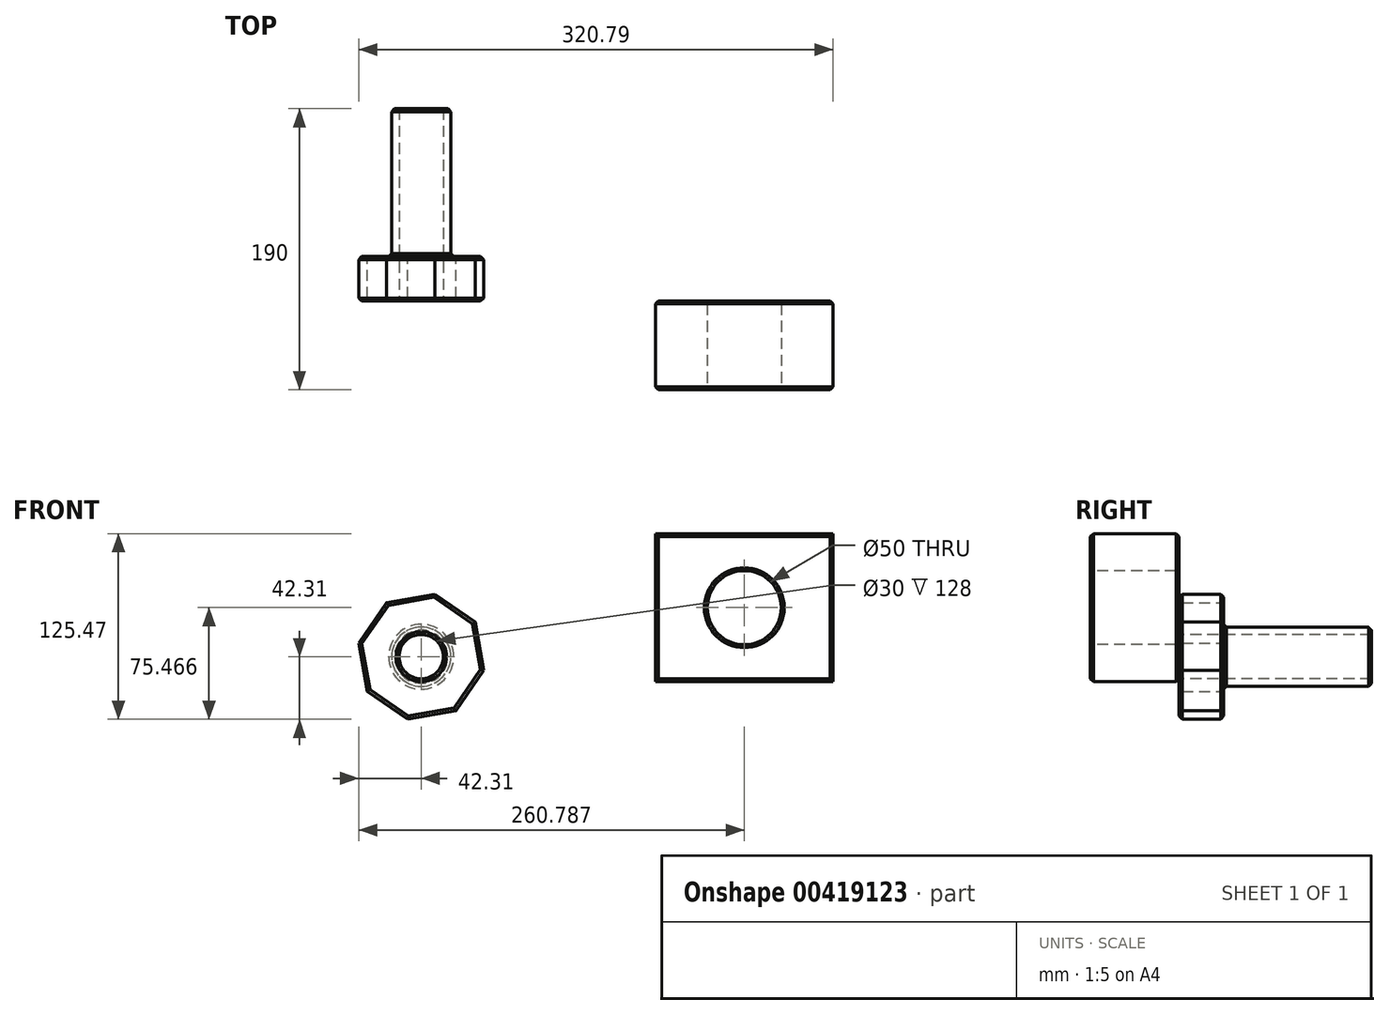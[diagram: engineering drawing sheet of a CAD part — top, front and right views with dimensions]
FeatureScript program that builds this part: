
annotation { "Feature Type Name" : "Feature", "Feature Type Description" : "" }
export const myFeature = defineFeature(function(context is Context, id is Id, definition is map)
    precondition{}
    {
        {
            var Q0;
            Q0=qCreatedBy(makeId("Front.planeOp"),FACE);
            var sketch = newSketch(context, id + "F0", { "sketchPlane" : qUnion([Q0])});
            skCircle(sketch, "E0.cCircle", {"center": v(0, 0) * mm, "radius": 40 * mm, "construction": true});
            skLineSegment(sketch, "E0.0", {"start": v(-42.31, 9.18) * mm, "end": v(-23.43, 36.4) * mm});
            skLineSegment(sketch, "E0.1", {"start": v(-23.43, 36.4) * mm, "end": v(9.18, 42.31) * mm});
            skLineSegment(sketch, "E0.2", {"start": v(9.18, 42.31) * mm, "end": v(36.4, 23.43) * mm});
            skLineSegment(sketch, "E0.3", {"start": v(36.4, 23.43) * mm, "end": v(42.31, -9.18) * mm});
            skLineSegment(sketch, "E0.4", {"start": v(42.31, -9.18) * mm, "end": v(23.43, -36.4) * mm});
            skLineSegment(sketch, "E0.5", {"start": v(23.43, -36.4) * mm, "end": v(-9.18, -42.31) * mm});
            skLineSegment(sketch, "E0.6", {"start": v(-9.18, -42.31) * mm, "end": v(-36.4, -23.43) * mm});
            skLineSegment(sketch, "E0.7", {"start": v(-36.4, -23.43) * mm, "end": v(-42.31, 9.18) * mm});
            skPoint(sketch, "E0.0.midPoint", {"position": v(-32.87, 22.8) * mm});
            skSolve(sketch);
        }
        {
            var Q0;
            Q0=makeQuery(id+"F0.imprint","IMPRINT",FACE,{"disambiguationData":[TD([[makeQuery(id+"F0.imprint","IMPRINT",EDGE,{"derivedFrom":sQuery(id+"F0.wireOp",EDGE,"E0.0")}),-1.0]])]});
            extrude(context, id + "F1", {"entities" : qUnion([Q0]), "depth" : 30 * mm});
        }
        {
            var Q0;
            Q0=makeQuery(id+"F1.opExtrude","CAP_FACE",FACE,{"disambiguationData":[OSD([sQuery(id+"F0.wireOp",EDGE,"E0.0"),sQuery(id+"F0.wireOp",EDGE,"E0.1"),sQuery(id+"F0.wireOp",EDGE,"E0.2"),sQuery(id+"F0.wireOp",EDGE,"E0.3"),sQuery(id+"F0.wireOp",EDGE,"E0.4"),sQuery(id+"F0.wireOp",EDGE,"E0.5"),sQuery(id+"F0.wireOp",EDGE,"E0.6"),sQuery(id+"F0.wireOp",EDGE,"E0.7")])],"isStart":true});
            var sketch = newSketch(context, id + "F2", { "sketchPlane" : qUnion([Q0])});
            skCircle(sketch, "E1", {"center": v(0, 0) * mm, "radius": 20 * mm});
            skSolve(sketch);
        }
        {
            var Q0;
            Q0=makeQuery(id+"F2.imprint","IMPRINT",FACE,{"disambiguationData":[TD([[makeQuery(id+"F2.imprint","IMPRINT",EDGE,{"derivedFrom":sQuery(id+"F2.wireOp",EDGE,"E1")}),1.0]])]});
            extrude(context, id + "F3", {"entities" : qUnion([Q0]), "operationType" : NewBodyOperationType.ADD, "depth" : 100 * mm});
        }
        {
            var Q0;
            Q0=makeQuery(id+"F1.opExtrude","CAP_FACE",FACE,{"disambiguationData":[OSD([sQuery(id+"F0.wireOp",EDGE,"E0.0"),sQuery(id+"F0.wireOp",EDGE,"E0.1"),sQuery(id+"F0.wireOp",EDGE,"E0.2"),sQuery(id+"F0.wireOp",EDGE,"E0.3"),sQuery(id+"F0.wireOp",EDGE,"E0.4"),sQuery(id+"F0.wireOp",EDGE,"E0.5"),sQuery(id+"F0.wireOp",EDGE,"E0.6"),sQuery(id+"F0.wireOp",EDGE,"E0.7")])],"isStart":false});
            var sketch = newSketch(context, id + "F4", { "sketchPlane" : qUnion([Q0])});
            skPoint(sketch, "E2", {"position": v(0, 0) * mm});
            skCircle(sketch, "E3", {"center": v(0, 0) * mm, "radius": 32.5 * mm});
            skSolve(sketch);
        }
        {
            var Q0;
            Q0=sQuery(id+"F4.wireOp",VERTEX,"E2");
            var Q1;
            Q1=makeQuery(id+"F1.opExtrude","SWEPT_BODY",BODY,{"disambiguationData":[OSD([sQuery(id+"F0.wireOp",EDGE,"E0.0"),sQuery(id+"F0.wireOp",EDGE,"E0.1"),sQuery(id+"F0.wireOp",EDGE,"E0.2"),sQuery(id+"F0.wireOp",EDGE,"E0.3"),sQuery(id+"F0.wireOp",EDGE,"E0.4"),sQuery(id+"F0.wireOp",EDGE,"E0.5"),sQuery(id+"F0.wireOp",EDGE,"E0.6"),sQuery(id+"F0.wireOp",EDGE,"E0.7")])]});
            hole(context, id + "F5", {"style" : HoleStyle.SIMPLE, "endStyle" : HoleEndStyle.THROUGH, "holeDiameter" : 30 * mm, "isTappedThrough" : true, "tappedDepth" : 12 * mm, "tapClearance" : 3, "locations" : qUnion([Q0]), "scope" : qUnion([Q1])});
        }
        {
            var Q0;
            Q0=makeQuery(id+"F5.hole-0.boolean.opBoolean","INTERSECT",EDGE,{"derivedFrom":[makeQuery(id+"F3.opExtrude","CAP_FACE",FACE,{"disambiguationData":[OSD([sQuery(id+"F2.wireOp",EDGE,"E1")])],"isStart":false}),makeQuery(id+"F5.hole-0.opRevolve","SWEPT_FACE",FACE,{"disambiguationData":[OSD([sQuery(id+"F5.hole-0.sketch.wireOp",EDGE,"core_line_2")])]})]});
            var Q1;
            Q1=makeQuery(id+"F3.opExtrude","CAP_EDGE",EDGE,{"disambiguationData":[OSD([sQuery(id+"F2.wireOp",EDGE,"E1")])],"isStart":false});
            chamfer(context, id + "F6", {"entities" : qUnion([Q0, Q1]), "width" : 2 * mm, "tangentPropagation" : true});
        }
        {
            var Q0;
            Q0=makeQuery(id+"F1.opExtrude","CAP_FACE",FACE,{"disambiguationData":[OSD([sQuery(id+"F0.wireOp",EDGE,"E0.0"),sQuery(id+"F0.wireOp",EDGE,"E0.1"),sQuery(id+"F0.wireOp",EDGE,"E0.2"),sQuery(id+"F0.wireOp",EDGE,"E0.3"),sQuery(id+"F0.wireOp",EDGE,"E0.4"),sQuery(id+"F0.wireOp",EDGE,"E0.5"),sQuery(id+"F0.wireOp",EDGE,"E0.6"),sQuery(id+"F0.wireOp",EDGE,"E0.7")])],"isStart":false});
            var sketch = newSketch(context, id + "F7", { "sketchPlane" : qUnion([Q0])});
            skLineSegment(sketch, "E4.bottom", {"start": v(158.48, 83.16) * mm, "end": v(278.48, 83.16) * mm});
            skLineSegment(sketch, "E4.top", {"start": v(158.48, -16.84) * mm, "end": v(278.48, -16.84) * mm});
            skLineSegment(sketch, "E4.left", {"start": v(158.48, 83.16) * mm, "end": v(158.48, -16.84) * mm});
            skLineSegment(sketch, "E4.right", {"start": v(278.48, 83.16) * mm, "end": v(278.48, -16.84) * mm});
            skSolve(sketch);
        }
        {
            var Q0;
            Q0=makeQuery(id+"F7.imprint","IMPRINT",FACE,{"disambiguationData":[TD([[makeQuery(id+"F7.imprint","IMPRINT",EDGE,{"derivedFrom":sQuery(id+"F7.wireOp",EDGE,"E4.bottom")}),-1.0]])]});
            extrude(context, id + "F8", {"entities" : qUnion([Q0]), "depth" : 60 * mm});
        }
        {
            var Q0;
            Q0=makeQuery(id+"F8.opExtrude","CAP_FACE",FACE,{"disambiguationData":[OSD([sQuery(id+"F7.wireOp",EDGE,"E4.bottom"),sQuery(id+"F7.wireOp",EDGE,"E4.top"),sQuery(id+"F7.wireOp",EDGE,"E4.left"),sQuery(id+"F7.wireOp",EDGE,"E4.right")])],"isStart":false});
            var sketch = newSketch(context, id + "F9", { "sketchPlane" : qUnion([Q0])});
            skPoint(sketch, "E5", {"position": v(218.48, 33.16) * mm});
            skSolve(sketch);
        }
        {
            var Q0;
            Q0=sQuery(id+"F9.wireOp",VERTEX,"E5");
            var Q1;
            Q1=makeQuery(id+"F8.opExtrude","SWEPT_BODY",BODY,{"disambiguationData":[OSD([sQuery(id+"F7.wireOp",EDGE,"E4.bottom"),sQuery(id+"F7.wireOp",EDGE,"E4.top"),sQuery(id+"F7.wireOp",EDGE,"E4.left"),sQuery(id+"F7.wireOp",EDGE,"E4.right")])]});
            hole(context, id + "F10", {"style" : HoleStyle.SIMPLE, "endStyle" : HoleEndStyle.THROUGH, "holeDiameter" : 50 * mm, "isTappedThrough" : true, "tappedDepth" : 12 * mm, "tapClearance" : 3, "locations" : qUnion([Q0]), "scope" : qUnion([Q1])});
        }
        {
            var Q0;
            Q0=makeQuery(id+"F8.opExtrude","CAP_FACE",FACE,{"disambiguationData":[OSD([sQuery(id+"F7.wireOp",EDGE,"E4.bottom"),sQuery(id+"F7.wireOp",EDGE,"E4.top"),sQuery(id+"F7.wireOp",EDGE,"E4.left"),sQuery(id+"F7.wireOp",EDGE,"E4.right")])],"isStart":false});
            chamfer(context, id + "F11", {"entities" : qUnion([Q0]), "width" : 2 * mm, "tangentPropagation" : true});
        }
        {
            var Q0;
            Q0=makeQuery(id+"F8.opExtrude","CAP_FACE",FACE,{"disambiguationData":[OSD([sQuery(id+"F7.wireOp",EDGE,"E4.bottom"),sQuery(id+"F7.wireOp",EDGE,"E4.top"),sQuery(id+"F7.wireOp",EDGE,"E4.left"),sQuery(id+"F7.wireOp",EDGE,"E4.right")])],"isStart":true});
            chamfer(context, id + "F12", {"entities" : qUnion([Q0]), "width" : 2 * mm, "tangentPropagation" : true});
        }
        {
            var Q0;
            Q0=makeQuery(id+"F1.opExtrude","CAP_FACE",FACE,{"disambiguationData":[OSD([sQuery(id+"F0.wireOp",EDGE,"E0.0"),sQuery(id+"F0.wireOp",EDGE,"E0.1"),sQuery(id+"F0.wireOp",EDGE,"E0.2"),sQuery(id+"F0.wireOp",EDGE,"E0.3"),sQuery(id+"F0.wireOp",EDGE,"E0.4"),sQuery(id+"F0.wireOp",EDGE,"E0.5"),sQuery(id+"F0.wireOp",EDGE,"E0.6"),sQuery(id+"F0.wireOp",EDGE,"E0.7")])],"isStart":false});
            chamfer(context, id + "F13", {"entities" : qUnion([Q0]), "width" : 2 * mm, "tangentPropagation" : true});
        }
        {
            var Q0;
            Q0=makeQuery(id+"F1.opExtrude","CAP_FACE",FACE,{"disambiguationData":[OSD([sQuery(id+"F0.wireOp",EDGE,"E0.0"),sQuery(id+"F0.wireOp",EDGE,"E0.1"),sQuery(id+"F0.wireOp",EDGE,"E0.2"),sQuery(id+"F0.wireOp",EDGE,"E0.3"),sQuery(id+"F0.wireOp",EDGE,"E0.4"),sQuery(id+"F0.wireOp",EDGE,"E0.5"),sQuery(id+"F0.wireOp",EDGE,"E0.6"),sQuery(id+"F0.wireOp",EDGE,"E0.7")])],"isStart":true});
            chamfer(context, id + "F14", {"entities" : qUnion([Q0]), "width" : 2 * mm, "tangentPropagation" : true});
        }
    });
